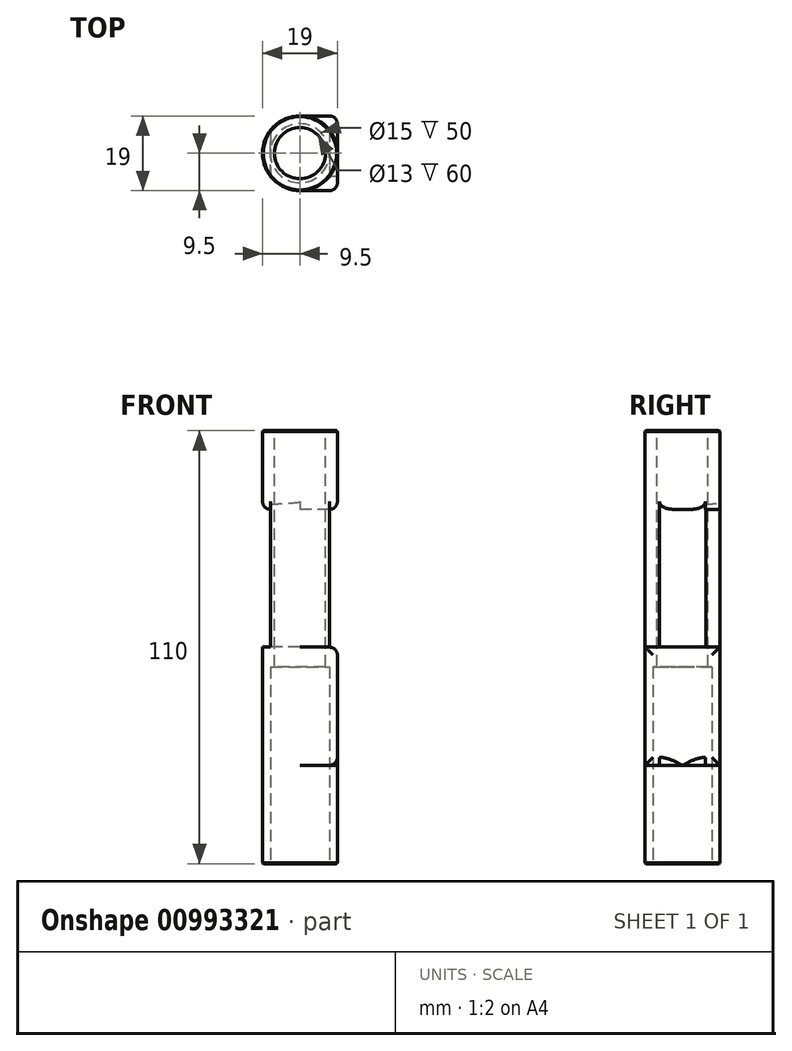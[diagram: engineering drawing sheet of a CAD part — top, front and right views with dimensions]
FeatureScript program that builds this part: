
annotation { "Feature Type Name" : "Feature", "Feature Type Description" : "" }
export const myFeature = defineFeature(function(context is Context, id is Id, definition is map)
    precondition{}
    {
        {
            var Q0;
            Q0=qCreatedBy(makeId("Top.planeOp"),FACE);
            var sketch = newSketch(context, id + "F0", { "sketchPlane" : qUnion([Q0])});
            skCircle(sketch, "E0", {"center": v(0, 0) * mm, "radius": 9.5 * mm});
            skSolve(sketch);
        }
        {
            var Q0;
            Q0 = qSketchRegion(id + "F0", true);
            extrude(context, id + "F1", {"entities" : qUnion([Q0]), "depth" : 25 * mm, "offsetDistance" : 25 * mm});
        }
        {
            var Q0;
            Q0=makeQuery(id+"F1.opExtrude","CAP_FACE",FACE,{"disambiguationData":[OSD([sQuery(id+"F0.wireOp",EDGE,"E0")])],"isStart":false});
            var sketch = newSketch(context, id + "F2", { "sketchPlane" : qUnion([Q0])});
            skLineSegment(sketch, "E1", {"start": v(0, 9.5) * mm, "end": v(9.5, 9.5) * mm});
            skLineSegment(sketch, "E2", {"start": v(9.5, 9.5) * mm, "end": v(9.5, -9.5) * mm});
            skLineSegment(sketch, "E3", {"start": v(9.5, -9.5) * mm, "end": v(0, -9.5) * mm});
            skArc(sketch, "E4", {"start": v(0, 9.5) * mm, "mid": v(-9.5, 0) * mm, "end": v(0, -9.5) * mm});
            skSolve(sketch);
        }
        {
            var Q0;
            Q0 = qSketchRegion(id + "F2", true);
            extrude(context, id + "F3", {"entities" : qUnion([Q0]), "operationType" : NewBodyOperationType.ADD, "depth" : 30 * mm, "offsetDistance" : 25 * mm});
        }
        {
            var Q0;
            Q0=makeQuery(id+"F3.opExtrude","CAP_FACE",FACE,{"disambiguationData":[OSD([sQuery(id+"F2.wireOp",EDGE,"1h4Q56GM-fo4D-TM5j-Uzqc-ZN7q8nBN5zEE"),sQuery(id+"F2.wireOp",EDGE,"E1"),sQuery(id+"F2.wireOp",EDGE,"E2"),sQuery(id+"F2.wireOp",EDGE,"E3")])],"isStart":false});
            var sketch = newSketch(context, id + "F4", { "sketchPlane" : qUnion([Q0])});
            skLineSegment(sketch, "E5", {"start": v(-7.5, 5.65) * mm, "end": v(-7.5, -5.83) * mm});
            skLineSegment(sketch, "E6", {"start": v(7.5, 6) * mm, "end": v(7.5, -5.83) * mm});
            skArc(sketch, "E7", {"start": v(7.5, 6) * mm, "mid": v(-0.08, 9.5) * mm, "end": v(-7.5, 5.65) * mm});
            skArc(sketch, "E8", {"start": v(-7.5, -5.83) * mm, "mid": v(0, -9.5) * mm, "end": v(7.5, -5.83) * mm});
            skSolve(sketch);
        }
        {
            var Q0;
            Q0 = qSketchRegion(id + "F4", true);
            extrude(context, id + "F5", {"entities" : qUnion([Q0]), "operationType" : NewBodyOperationType.ADD, "depth" : 35 * mm, "offsetDistance" : 25 * mm});
        }
        {
            var Q0;
            Q0=makeQuery(id+"F5.opExtrude","CAP_FACE",FACE,{"disambiguationData":[OSD([sQuery(id+"F4.wireOp",EDGE,"E5"),sQuery(id+"F4.wireOp",EDGE,"E6"),sQuery(id+"F4.wireOp",EDGE,"E7"),sQuery(id+"F4.wireOp",EDGE,"E8")])],"isStart":false});
            var sketch = newSketch(context, id + "F6", { "sketchPlane" : qUnion([Q0])});
            skCircle(sketch, "E9", {"center": v(0, 0) * mm, "radius": 9.5 * mm});
            skSolve(sketch);
        }
        {
            var Q0;
            Q0 = qSketchRegion(id + "F6", true);
            extrude(context, id + "F7", {"entities" : qUnion([Q0]), "operationType" : NewBodyOperationType.ADD, "depth" : 20 * mm, "offsetDistance" : 25 * mm});
        }
        {
            var Q0;
            {var subQ0=sQuery(id+"F4.wireOp",EDGE,"E6");var subQ1=sQuery(id+"F6.wireOp",EDGE,"E9");var subQ2=makeQuery(id+"F7.opExtrude","SWEPT_FACE",FACE,{"disambiguationData":[OSD([subQ1])]});var subQ3=makeQuery(id+"F7.opExtrude","CAP_FACE",FACE,{"disambiguationData":[OSD([subQ1])],"isStart":true});Q0=makeQuery(id+"F7.boolean.opBoolean","SPLIT",EDGE,{"disambiguationData":[topologyDisambiguationEdgeConnected([subQ2,subQ3]),TD([makeQuery(id+"F5.opExtrude","SWEPT_FACE",FACE,{"disambiguationData":[OSD([subQ0])]})])],"derivedFrom":makeQuery(id+"F7.opExtrude","CAP_EDGE",EDGE,{"disambiguationData":[OSD([subQ1])],"isStart":true})});}
            var Q1;
            {var subQ0=sQuery(id+"F6.wireOp",EDGE,"E9");var subQ1=makeQuery(id+"F7.opExtrude","SWEPT_FACE",FACE,{"disambiguationData":[OSD([subQ0])]});var subQ3=sQuery(id+"F4.wireOp",EDGE,"E5");var subQ4=makeQuery(id+"F7.opExtrude","CAP_FACE",FACE,{"disambiguationData":[OSD([subQ0])],"isStart":true});Q1=makeQuery(id+"F7.boolean.opBoolean","SPLIT",EDGE,{"disambiguationData":[topologyDisambiguationEdgeConnected([subQ1,subQ4]),TD([makeQuery(id+"F5.opExtrude","SWEPT_FACE",FACE,{"disambiguationData":[OSD([subQ3])]})])],"derivedFrom":makeQuery(id+"F7.opExtrude","CAP_EDGE",EDGE,{"disambiguationData":[OSD([subQ0])],"isStart":true})});}
            var Q2;
            Q2=makeQuery(id+"F3.opExtrude","CAP_EDGE",EDGE,{"disambiguationData":[OSD([sQuery(id+"F2.wireOp",EDGE,"E2")])],"isStart":false});
            var Q3;
            Q3=makeQuery(id+"F3.opExtrude","SWEPT_EDGE",EDGE,{"disambiguationData":[OSD([sQuery(id+"F2.wireOp",EDGE,"E2"),sQuery(id+"F2.wireOp",EDGE,"E3")])]});
            var Q4;
            Q4=makeQuery(id+"F3.opExtrude","SWEPT_EDGE",EDGE,{"disambiguationData":[OSD([sQuery(id+"F2.wireOp",EDGE,"E1"),sQuery(id+"F2.wireOp",EDGE,"E2")])]});
            var Q5;
            {var subQ0=sQuery(id+"F2.wireOp",EDGE,"E3");var subQ1=sQuery(id+"F2.wireOp",EDGE,"E2");Q5=makeQuery(id+"F3.boolean.opBoolean","SPLIT",EDGE,{"disambiguationData":[TD([makeQuery(id+"F3.opExtrude","SWEPT_FACE",FACE,{"disambiguationData":[OSD([subQ0])]})])],"derivedFrom":makeQuery(id+"F3.opExtrude","CAP_EDGE",EDGE,{"disambiguationData":[OSD([subQ1])],"isStart":true})});}
            fillet(context, id + "F8", {"entities" : qUnion([Q0, Q1, Q2, Q3, Q4, Q5]), "radius" : 2 * mm, "tangentPropagation" : true, "allowEdgeOverflow" : false});
        }
        {
            var Q0;
            Q0=makeQuery(id+"F1.opExtrude","CAP_FACE",FACE,{"disambiguationData":[OSD([sQuery(id+"F0.wireOp",EDGE,"E0")])],"isStart":true});
            var sketch = newSketch(context, id + "F9", { "sketchPlane" : qUnion([Q0])});
            skCircle(sketch, "E10", {"center": v(0, 0) * mm, "radius": 7.5 * mm});
            skSolve(sketch);
        }
        {
            var Q0;
            Q0 = qSketchRegion(id + "F9", true);
            extrude(context, id + "F10", {"entities" : qUnion([Q0]), "operationType" : NewBodyOperationType.REMOVE, "oppositeDirection" : true, "depth" : 50 * mm, "offsetDistance" : 25 * mm});
        }
        {
            var Q0;
            Q0=makeQuery(id+"F7.opExtrude","CAP_FACE",FACE,{"disambiguationData":[OSD([sQuery(id+"F6.wireOp",EDGE,"E9")])],"isStart":false});
            var sketch = newSketch(context, id + "F11", { "sketchPlane" : qUnion([Q0])});
            skCircle(sketch, "E11", {"center": v(0, 0) * mm, "radius": 6.5 * mm});
            skSolve(sketch);
        }
        {
            var Q0;
            Q0 = qSketchRegion(id + "F11", true);
            extrude(context, id + "F12", {"entities" : qUnion([Q0]), "operationType" : NewBodyOperationType.REMOVE, "oppositeDirection" : true, "depth" : 60 * mm, "offsetDistance" : 25 * mm});
        }
        {
            var Q0;
            Q0=makeQuery(id+"F7.opExtrude","CAP_EDGE",EDGE,{"disambiguationData":[OSD([sQuery(id+"F6.wireOp",EDGE,"E9")])],"isStart":false});
            var Q1;
            Q1=makeQuery(id+"F1.opExtrude","CAP_EDGE",EDGE,{"disambiguationData":[OSD([sQuery(id+"F0.wireOp",EDGE,"E0")])],"isStart":true});
            chamfer(context, id + "F13", {"entities" : qUnion([Q0, Q1]), "width" : .2 * mm, "tangentPropagation" : true});
        }
    });
